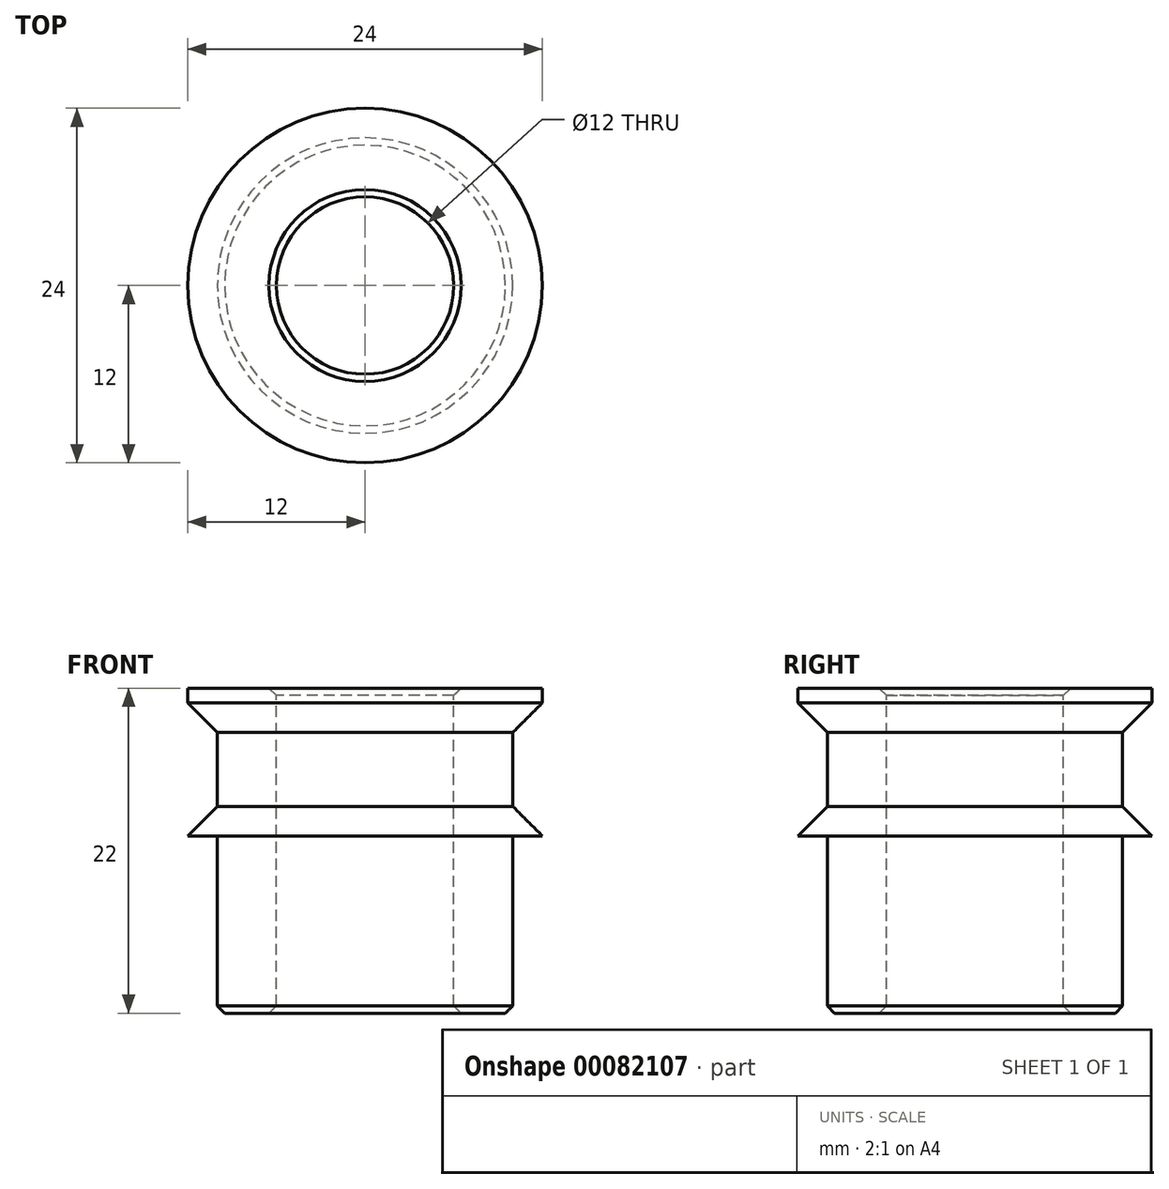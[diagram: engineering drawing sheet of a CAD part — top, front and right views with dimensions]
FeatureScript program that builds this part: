
annotation { "Feature Type Name" : "Feature", "Feature Type Description" : "" }
export const myFeature = defineFeature(function(context is Context, id is Id, definition is map)
    precondition{}
    {
        {
            var Q0;
            Q0=qCreatedBy(makeId("Top.planeOp"),FACE);
            var sketch = newSketch(context, id + "F0", { "sketchPlane" : qUnion([Q0])});
            skCircle(sketch, "E0", {"center": v(0, 0) * mm, "radius": 10 * mm});
            skCircle(sketch, "E1", {"center": v(0, 0) * mm, "radius": 6 * mm});
            skSolve(sketch);
        }
        {
            var Q0;
            Q0 = qSketchRegion(id + "F0", true);
            extrude(context, id + "F1", {"entities" : qUnion([Q0]), "oppositeDirection" : true, "depth" : 12 * mm});
        }
        {
            var Q0;
            Q0=makeQuery(id+"F1.opExtrude","CAP_FACE",FACE,{"disambiguationData":[OSD([sQuery(id+"F0.wireOp",EDGE,"E0"),sQuery(id+"F0.wireOp",EDGE,"E1")])],"isStart":true});
            var sketch = newSketch(context, id + "F2", { "sketchPlane" : qUnion([Q0])});
            skCircle(sketch, "E2.0", {"center": v(0, 0) * mm, "radius": 6 * mm});
            skCircle(sketch, "E3", {"center": v(0, 0) * mm, "radius": 12 * mm});
            skSolve(sketch);
        }
        {
            var Q0;
            Q0 = qSketchRegion(id + "F2", true);
            extrude(context, id + "F3", {"entities" : qUnion([Q0]), "operationType" : NewBodyOperationType.ADD, "depth" : 2 * mm});
        }
        {
            var Q0;
            Q0=makeQuery(id+"F3.opExtrude","CAP_FACE",FACE,{"disambiguationData":[OSD([sQuery(id+"F2.wireOp",EDGE,"E2.0"),sQuery(id+"F2.wireOp",EDGE,"E3")])],"isStart":false});
            var sketch = newSketch(context, id + "F4", { "sketchPlane" : qUnion([Q0])});
            skCircle(sketch, "E4.0", {"center": v(0, 0) * mm, "radius": 6 * mm});
            skCircle(sketch, "E5", {"center": v(0, 0) * mm, "radius": 10 * mm});
            skSolve(sketch);
        }
        {
            var Q0;
            Q0 = qSketchRegion(id + "F4", true);
            extrude(context, id + "F5", {"entities" : qUnion([Q0]), "operationType" : NewBodyOperationType.ADD, "depth" : 5 * mm});
        }
        {
            var Q0;
            Q0=makeQuery(id+"F5.opExtrude","CAP_FACE",FACE,{"disambiguationData":[OSD([sQuery(id+"F4.wireOp",EDGE,"E4.0"),sQuery(id+"F4.wireOp",EDGE,"E5")])],"isStart":false});
            var sketch = newSketch(context, id + "F6", { "sketchPlane" : qUnion([Q0])});
            skCircle(sketch, "E6.0", {"center": v(0, 0) * mm, "radius": 6 * mm});
            skCircle(sketch, "E7.0", {"center": v(0, 0) * mm, "radius": 12 * mm});
            skSolve(sketch);
        }
        {
            var Q0;
            Q0 = qSketchRegion(id + "F6", true);
            extrude(context, id + "F7", {"entities" : qUnion([Q0]), "operationType" : NewBodyOperationType.ADD, "depth" : 3 * mm});
        }
        {
            var Q0;
            Q0=makeQuery(id+"F3.opExtrude","CAP_EDGE",EDGE,{"disambiguationData":[OSD([sQuery(id+"F2.wireOp",EDGE,"E3")])],"isStart":false});
            chamfer(context, id + "F8", {"entities" : qUnion([Q0]), "width" : 2 * mm, "tangentPropagation" : true});
        }
        {
            var Q0;
            Q0=makeQuery(id+"F7.opExtrude","CAP_EDGE",EDGE,{"disambiguationData":[OSD([sQuery(id+"F6.wireOp",EDGE,"E7.0")])],"isStart":true});
            chamfer(context, id + "F9", {"entities" : qUnion([Q0]), "width" : 2 * mm, "tangentPropagation" : true});
        }
        {
            var Q0;
            Q0=makeQuery(id+"F1.opExtrude","CAP_FACE",FACE,{"disambiguationData":[OSD([sQuery(id+"F0.wireOp",EDGE,"E0"),sQuery(id+"F0.wireOp",EDGE,"E1")])],"isStart":false});
            var Q1;
            Q1=makeQuery(id+"F7.opExtrude","CAP_EDGE",EDGE,{"disambiguationData":[OSD([sQuery(id+"F6.wireOp",EDGE,"E6.0")])],"isStart":false});
            chamfer(context, id + "F10", {"entities" : qUnion([Q0, Q1]), "width" : 0.5 * mm, "tangentPropagation" : true});
        }
    });
